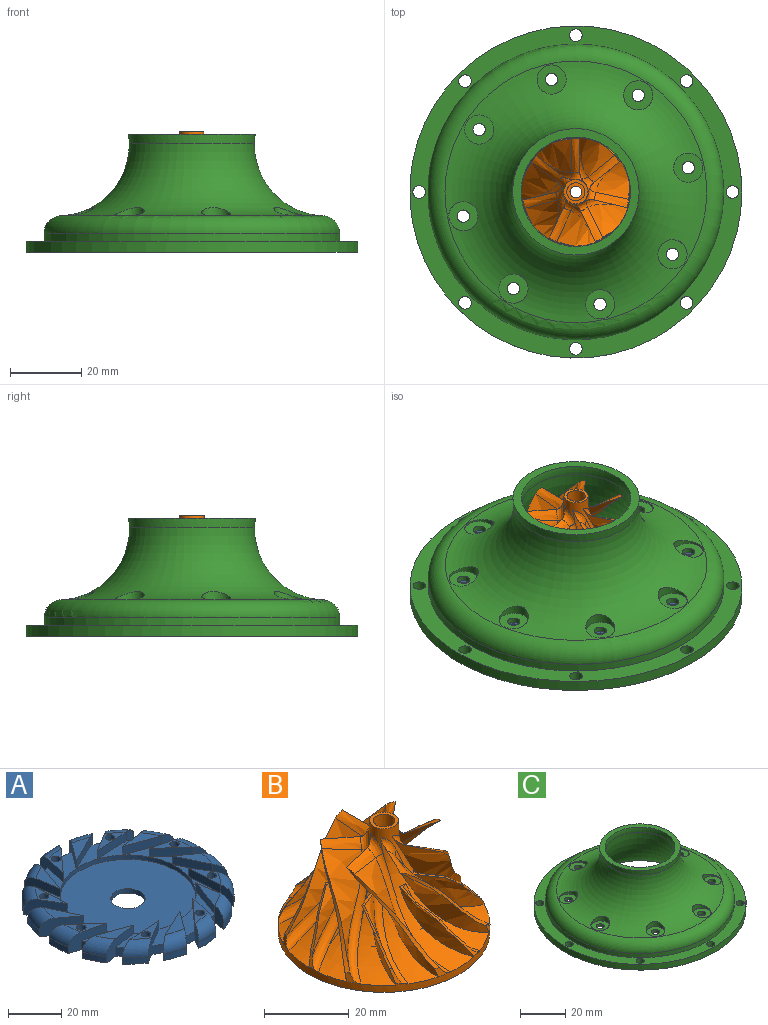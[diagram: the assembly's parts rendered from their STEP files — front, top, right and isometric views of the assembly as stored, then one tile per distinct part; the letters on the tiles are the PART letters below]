
ASSEMBLY  parts=3 mates=1
PART A: 140 faces, bbox 81x81x7.9 mm
  f0: plane 80x80mm, normal (0,0,-1), area 4366.8mm2, adj f1,f2,f3,f4,f5,f6,f7,f8
  f1: cylinder r=35mm len=4.02mm, axis (0,0,1), area 21.5mm2, adj f0,f17,f64,f85
  f2: cylinder r=35mm len=5.08mm, axis (0,0,1), area 21.5mm2, adj f0,f19,f62,f84
  f3: cylinder r=35mm len=5.37mm, axis (0,0,1), area 21.5mm2, adj f0,f20,f60,f99
  f4: cylinder r=35mm len=4.85mm, axis (0,0,1), area 21.5mm2, adj f0,f21,f58,f98
  f5: cylinder r=35mm len=4.02mm, axis (0,0,1), area 21.5mm2, adj f0,f22,f56,f97
  f6: cylinder r=35mm len=5.08mm, axis (0,0,1), area 21.5mm2, adj f0,f23,f54,f96
  f7: cylinder r=35mm len=5.37mm, axis (0,0,1), area 21.5mm2, adj f0,f24,f52,f95
  f8: cylinder r=35mm len=4.85mm, axis (0,0,1), area 21.5mm2, adj f0,f25,f50,f94
  f9: cylinder r=35mm len=4.02mm, axis (0,0,1), area 21.5mm2, adj f0,f26,f48,f93
  f10: cylinder r=35mm len=5.08mm, axis (0,0,1), area 21.5mm2, adj f0,f27,f46,f92
  f11: cylinder r=35mm len=5.37mm, axis (0,0,1), area 21.5mm2, adj f0,f28,f44,f91
  f12: cylinder r=35mm len=4.85mm, axis (0,0,1), area 21.5mm2, adj f0,f29,f42,f90
  f13: cylinder r=35mm len=4.02mm, axis (0,0,1), area 21.5mm2, adj f0,f30,f40,f89
  f14: cylinder r=35mm len=5.08mm, axis (0,0,1), area 21.5mm2, adj f0,f31,f38,f88
  f15: cylinder r=35mm len=5.37mm, axis (0,0,1), area 21.5mm2, adj f0,f32,f36,f87
  f16: cylinder r=35mm len=4.85mm, axis (0,0,1), area 21.5mm2, adj f0,f18,f66,f86
  f17: plane 19.86x5.71mm, normal (0,0,1), area 65.9mm2, adj f1,f35,f64,f67
  f18: plane 19.57x8.16mm, normal (0,0,1), area 65.9mm2, adj f16,f35,f37,f66
  f19: plane 17.11x10.57mm, normal (0,0,1), area 65.9mm2, adj f2,f35,f62,f65
  f20: plane 16.31x12.08mm, normal (0,0,1), area 65.9mm2, adj f3,f35,f60,f63
  f21: plane 19.57x8.16mm, normal (0,0,1), area 65.9mm2, adj f4,f35,f58,f61
  f22: plane 19.86x5.71mm, normal (0,0,1), area 65.9mm2, adj f5,f35,f56,f59
  f23: plane 17.11x10.57mm, normal (0,0,1), area 65.9mm2, adj f6,f35,f54,f57
  f24: plane 16.31x12.08mm, normal (0,0,1), area 65.9mm2, adj f7,f35,f52,f55
  f25: plane 19.57x8.16mm, normal (0,0,1), area 65.9mm2, adj f8,f35,f50,f53
  f26: plane 19.86x5.71mm, normal (0,0,1), area 65.9mm2, adj f9,f35,f48,f51
  f27: plane 17.11x10.57mm, normal (0,0,1), area 65.9mm2, adj f10,f35,f46,f49
  f28: plane 16.31x12.08mm, normal (0,0,1), area 65.9mm2, adj f11,f35,f44,f47
  f29: plane 19.57x8.16mm, normal (0,0,1), area 65.9mm2, adj f12,f35,f42,f45
  f30: plane 19.86x5.71mm, normal (0,0,1), area 65.9mm2, adj f13,f35,f40,f43
  f31: plane 17.11x10.57mm, normal (0,0,1), area 65.9mm2, adj f14,f35,f38,f41
  f32: plane 16.31x12.08mm, normal (0,0,1), area 65.9mm2, adj f15,f35,f36,f39
  f33: plane 51.42x51.42mm, normal (0,0,1), area 1943.8mm2, adj f34,f35
  f34: cylinder r=6.5mm len=13mm, axis (0,0,1), area 81.7mm2, adj f0,f33
  f35: cylinder r=25.71mm len=51.42mm, axis (0,0,-1), area 323.1mm2, adj f17,f18,f19,f20,f21,f22,f23,f24
  f36: plane 13.56x9.97mm, normal (-0.59,-0.81,0), area 82.1mm2, adj f0,f15,f32,f37,f68,f109,f127
  f37: plane 14.73x6.97mm, normal (0.9,0.43,0), area 63.5mm2, adj f18,f36,f86,f109
  f38: plane 16.35x7.9mm, normal (-0.24,-0.97,0), area 82.1mm2, adj f0,f14,f31,f39,f69,f117,f126
  f39: plane 12.07x10.94mm, normal (0.67,0.74,0), area 63.5mm2, adj f32,f38,f87,f117
  f40: plane 16.64x7.9mm, normal (0.15,-0.99,0), area 82.1mm2, adj f0,f13,f30,f41,f70,f110,f125
  f41: plane 15.34x5.49mm, normal (0.34,0.94,0), area 63.5mm2, adj f31,f40,f88,f110
  f42: plane 14.4x8.72mm, normal (0.52,-0.86,0), area 82.1mm2, adj f0,f12,f29,f43,f71,f118,f124
  f43: plane 16.27x3.9mm, normal (-0.05,1,0), area 63.5mm2, adj f30,f42,f89,f118
  f44: plane 13.56x9.97mm, normal (0.81,-0.59,0), area 82.1mm2, adj f0,f11,f28,f45,f72,f111,f139
  f45: plane 14.73x6.97mm, normal (-0.43,0.9,0), area 63.5mm2, adj f29,f44,f90,f111
  f46: plane 16.35x7.9mm, normal (0.97,-0.24,0), area 82.1mm2, adj f0,f10,f27,f47,f73,f119,f138
  f47: plane 12.07x10.94mm, normal (-0.74,0.67,0), area 63.5mm2, adj f28,f46,f91,f119
  f48: plane 16.64x7.9mm, normal (0.99,0.15,0), area 82.1mm2, adj f0,f9,f26,f49,f74,f112,f137
  f49: plane 15.34x5.49mm, normal (-0.94,0.34,0), area 63.5mm2, adj f27,f48,f92,f112
  f50: plane 14.4x8.72mm, normal (0.86,0.52,0), area 82.1mm2, adj f0,f8,f25,f51,f75,f120,f136
  f51: plane 16.27x3.9mm, normal (-1,-0.05,0), area 63.5mm2, adj f26,f50,f93,f120
  f52: plane 13.56x9.97mm, normal (0.59,0.81,0), area 82.1mm2, adj f0,f7,f24,f53,f76,f113,f135
  f53: plane 14.73x6.97mm, normal (-0.9,-0.43,0), area 63.5mm2, adj f25,f52,f94,f113
  f54: plane 16.35x7.9mm, normal (0.24,0.97,0), area 82.1mm2, adj f0,f6,f23,f55,f77,f121,f134
  f55: plane 12.07x10.94mm, normal (-0.67,-0.74,0), area 63.5mm2, adj f24,f54,f95,f121
  f56: plane 16.64x7.9mm, normal (-0.15,0.99,0), area 82.1mm2, adj f0,f5,f22,f57,f78,f114,f133
  f57: plane 15.34x5.49mm, normal (-0.34,-0.94,0), area 63.5mm2, adj f23,f56,f96,f114
  f58: plane 14.4x8.72mm, normal (-0.52,0.86,0), area 82.1mm2, adj f0,f4,f21,f59,f79,f122,f132
  f59: plane 16.27x3.9mm, normal (0.05,-1,0), area 63.5mm2, adj f22,f58,f97,f122
  f60: plane 13.56x9.97mm, normal (-0.81,0.59,0), area 82.1mm2, adj f0,f3,f20,f61,f80,f115,f131
  f61: plane 14.73x6.97mm, normal (0.43,-0.9,0), area 63.5mm2, adj f21,f60,f98,f115
  f62: plane 16.35x7.9mm, normal (-0.97,0.24,0), area 82.1mm2, adj f0,f2,f19,f63,f81,f123,f130
  f63: plane 12.07x10.94mm, normal (0.74,-0.67,0), area 63.5mm2, adj f20,f62,f99,f123
  f64: plane 16.64x7.9mm, normal (-0.99,-0.15,0), area 82.1mm2, adj f0,f1,f17,f65,f82,f108,f129
  f65: plane 15.34x5.49mm, normal (0.94,-0.34,0), area 63.5mm2, adj f19,f64,f84,f108
  f66: plane 14.4x8.72mm, normal (-0.86,-0.52,0), area 82.1mm2, adj f0,f16,f18,f67,f83,f116,f128
  f67: plane 16.27x3.9mm, normal (1,0.05,0), area 63.5mm2, adj f17,f66,f85,f116
  f68: cylinder r=40mm len=9.3mm, axis (0,0,-1), area 28.5mm2, adj f0,f36,f86,f127
  f69: cylinder r=40mm len=9.79mm, axis (0,0,-1), area 28.5mm2, adj f0,f38,f87,f126
  f70: cylinder r=40mm len=8.79mm, axis (0,0,-1), area 28.5mm2, adj f0,f40,f88,f125
  f71: cylinder r=40mm len=7.4mm, axis (0,0,-1), area 28.5mm2, adj f0,f42,f89,f124
  f72: cylinder r=40mm len=9.3mm, axis (0,0,-1), area 28.5mm2, adj f0,f44,f90,f139
  f73: cylinder r=40mm len=9.79mm, axis (0,0,-1), area 28.5mm2, adj f0,f46,f91,f138
  f74: cylinder r=40mm len=8.79mm, axis (0,0,-1), area 28.5mm2, adj f0,f48,f92,f137
  f75: cylinder r=40mm len=7.4mm, axis (0,0,-1), area 28.5mm2, adj f0,f50,f93,f136
  f76: cylinder r=40mm len=9.3mm, axis (0,0,-1), area 28.5mm2, adj f0,f52,f94,f135
  f77: cylinder r=40mm len=9.79mm, axis (0,0,-1), area 28.5mm2, adj f0,f54,f95,f134
  f78: cylinder r=40mm len=8.79mm, axis (0,0,-1), area 28.5mm2, adj f0,f56,f96,f133
  f79: cylinder r=40mm len=7.4mm, axis (0,0,-1), area 28.5mm2, adj f0,f58,f97,f132
  f80: cylinder r=40mm len=9.3mm, axis (0,0,-1), area 28.5mm2, adj f0,f60,f98,f131
  f81: cylinder r=40mm len=9.79mm, axis (0,0,-1), area 28.5mm2, adj f0,f62,f99,f130
  f82: cylinder r=40mm len=8.79mm, axis (0,0,-1), area 28.5mm2, adj f0,f64,f84,f129
  f83: cylinder r=40mm len=7.4mm, axis (0,0,-1), area 28.5mm2, adj f0,f66,f85,f128
  f84: plane 7.9x5.67mm, normal (0.99,-0.13,0), area 39.1mm2, adj f0,f2,f65,f82,f129
  f85: plane 7.9x5.53mm, normal (0.97,0.26,0), area 39.1mm2, adj f0,f1,f67,f83,f128
  f86: plane 7.9x4.54mm, normal (0.79,0.61,0), area 39.1mm2, adj f0,f16,f37,f68,f127
  f87: plane 7.9x4.95mm, normal (0.5,0.87,0), area 39.1mm2, adj f0,f15,f39,f69,f126
  f88: plane 7.9x5.67mm, normal (0.13,0.99,0), area 39.1mm2, adj f0,f14,f41,f70,f125
  f89: plane 7.9x5.53mm, normal (-0.26,0.97,0), area 39.1mm2, adj f0,f13,f43,f71,f124
  f90: plane 7.9x4.54mm, normal (-0.61,0.79,0), area 39.1mm2, adj f0,f12,f45,f72,f139
  f91: plane 7.9x4.95mm, normal (-0.87,0.5,0), area 39.1mm2, adj f0,f11,f47,f73,f138
  f92: plane 7.9x5.67mm, normal (-0.99,0.13,0), area 39.1mm2, adj f0,f10,f49,f74,f137
  f93: plane 7.9x5.53mm, normal (-0.97,-0.26,0), area 39.1mm2, adj f0,f9,f51,f75,f136
  f94: plane 7.9x4.54mm, normal (-0.79,-0.61,0), area 39.1mm2, adj f0,f8,f53,f76,f135
  f95: plane 7.9x4.95mm, normal (-0.5,-0.87,0), area 39.1mm2, adj f0,f7,f55,f77,f134
  f96: plane 7.9x5.67mm, normal (-0.13,-0.99,0), area 39.1mm2, adj f0,f6,f57,f78,f133
  f97: plane 7.9x5.53mm, normal (0.26,-0.97,0), area 39.1mm2, adj f0,f5,f59,f79,f132
  f98: plane 7.9x4.54mm, normal (0.61,-0.79,0), area 39.1mm2, adj f0,f4,f61,f80,f131
  f99: plane 7.9x4.95mm, normal (0.87,-0.5,0), area 39.1mm2, adj f0,f3,f63,f81,f130
  f100: cylinder r=1.75mm len=7.9mm, axis (0,0,1), area 86.9mm2, adj f0,f116
  f101: cylinder r=1.75mm len=7.9mm, axis (0,0,1), area 86.9mm2, adj f0,f123
  f102: cylinder r=1.75mm len=7.9mm, axis (0,0,1), area 86.9mm2, adj f0,f122
  f103: cylinder r=1.75mm len=7.9mm, axis (0,0,1), area 86.9mm2, adj f0,f121
  f104: cylinder r=1.75mm len=7.9mm, axis (0,0,1), area 86.9mm2, adj f0,f120
  f105: cylinder r=1.75mm len=7.9mm, axis (0,0,1), area 86.9mm2, adj f0,f119
  f106: cylinder r=1.75mm len=7.9mm, axis (0,0,1), area 86.9mm2, adj f0,f118
  f107: cylinder r=1.75mm len=7.9mm, axis (0,0,1), area 86.9mm2, adj f0,f117
  f108: plane 15.34x7.18mm, normal (0,0,1), area 44.9mm2, adj f64,f65,f129
  f109: plane 14.73x9.06mm, normal (0,0,1), area 44.9mm2, adj f36,f37,f127
  f110: plane 15.34x7.18mm, normal (0,0,1), area 44.9mm2, adj f40,f41,f125
  f111: plane 14.73x9.06mm, normal (0,0,1), area 44.9mm2, adj f44,f45,f139
  f112: plane 15.34x7.18mm, normal (0,0,1), area 44.9mm2, adj f48,f49,f137
  f113: plane 14.73x9.06mm, normal (0,0,1), area 44.9mm2, adj f52,f53,f135
  f114: plane 15.34x7.18mm, normal (0,0,1), area 44.9mm2, adj f56,f57,f133
  f115: plane 14.73x9.06mm, normal (0,0,1), area 44.9mm2, adj f60,f61,f131
  f116: plane 16.27x5.82mm, normal (0,0,1), area 35.3mm2, adj f66,f67,f100,f128
  f117: plane 12.07x10.94mm, normal (0,0,1), area 35.3mm2, adj f38,f39,f107,f126
  f118: plane 16.27x5.82mm, normal (0,0,1), area 35.3mm2, adj f42,f43,f106,f124
  f119: plane 12.07x10.94mm, normal (0,0,1), area 35.3mm2, adj f46,f47,f105,f138
  f120: plane 16.27x5.82mm, normal (0,0,1), area 35.3mm2, adj f50,f51,f104,f136
  f121: plane 12.07x10.94mm, normal (0,0,1), area 35.3mm2, adj f54,f55,f103,f134
  f122: plane 16.27x5.82mm, normal (0,0,1), area 35.3mm2, adj f58,f59,f102,f132
  f123: plane 12.07x10.94mm, normal (0,0,1), area 35.3mm2, adj f62,f63,f101,f130
  f124: torus R=35mm, axis (0,0,1), area 73.1mm2, adj f42,f71,f89,f118
  f125: torus R=35mm, axis (0,0,1), area 73.1mm2, adj f40,f70,f88,f110
  f126: torus R=35mm, axis (0,0,1), area 73.1mm2, adj f38,f69,f87,f117
  f127: torus R=35mm, axis (0,0,1), area 73.1mm2, adj f36,f68,f86,f109
  f128: torus R=35mm, axis (0,0,1), area 73.1mm2, adj f66,f83,f85,f116
  f129: torus R=35mm, axis (0,0,1), area 73.1mm2, adj f64,f82,f84,f108
  f130: torus R=35mm, axis (0,0,1), area 73.1mm2, adj f62,f81,f99,f123
  f131: torus R=35mm, axis (0,0,1), area 73.1mm2, adj f60,f80,f98,f115
  f132: torus R=35mm, axis (0,0,1), area 73.1mm2, adj f58,f79,f97,f122
  f133: torus R=35mm, axis (0,0,1), area 73.1mm2, adj f56,f78,f96,f114
  f134: torus R=35mm, axis (0,0,1), area 73.1mm2, adj f54,f77,f95,f121
  f135: torus R=35mm, axis (0,0,1), area 73.1mm2, adj f52,f76,f94,f113
  f136: torus R=35mm, axis (0,0,1), area 73.1mm2, adj f50,f75,f93,f120
  f137: torus R=35mm, axis (0,0,1), area 73.1mm2, adj f48,f74,f92,f112
  f138: torus R=35mm, axis (0,0,1), area 73.1mm2, adj f46,f73,f91,f119
  f139: torus R=35mm, axis (0,0,1), area 73.1mm2, adj f44,f72,f90,f111
PART B: 110 faces, bbox 96.8x96.8x57.1 mm
  f0: bspline ~8.36x7mm, area 3.9mm2, adj f7,f20,f39,f50,f76
  f1: bspline ~8.36x7.68mm, area 3.9mm2, adj f8,f19,f39,f53,f75
  f2: bspline ~3.52x3.19mm, area 3.9mm2, adj f9,f18,f39,f56,f74
  f3: bspline ~8.36x6.86mm, area 3.9mm2, adj f10,f17,f39,f59,f73
  f4: bspline ~8.36x8.15mm, area 3.9mm2, adj f11,f16,f39,f62,f72
  f5: bspline ~8.36x5.88mm, area 3.5mm2, adj f12,f15,f39,f40,f65,f71
  f6: bspline ~3.37x3.19mm, area 3.9mm2, adj f13,f14,f39,f68,f70
  f7: bspline ~20.21x15mm, area 105.9mm2, adj f0,f39,f43,f49,f51,f76
  f8: bspline ~20.21x15mm, area 105.9mm2, adj f1,f39,f43,f52,f54,f75
  f9: bspline ~18.13x15mm, area 105.9mm2, adj f2,f39,f43,f55,f57,f74
  f10: bspline ~19.19x15mm, area 105.9mm2, adj f3,f39,f43,f58,f60,f73
  f11: bspline ~15x14.27mm, area 105.9mm2, adj f4,f39,f43,f61,f63,f72
  f12: bspline ~18.97x15mm, area 105.9mm2, adj f5,f40,f43,f64,f66,f71
  f13: bspline ~18.13x15mm, area 105.9mm2, adj f6,f39,f42,f67,f69,f70
  f14: bspline ~18.5x17.17mm, area 69.7mm2, adj f6,f39,f42,f67,f68
  f15: bspline ~20.78x17.17mm, area 69.7mm2, adj f5,f39,f43,f44,f64,f65
  f16: bspline ~17.35x16.96mm, area 69.7mm2, adj f4,f39,f43,f61,f62
  f17: bspline ~21.06x17.17mm, area 69.7mm2, adj f3,f39,f43,f58,f59
  f18: bspline ~17.85x17.35mm, area 69.7mm2, adj f2,f39,f43,f55,f56
  f19: bspline ~20.29x17.17mm, area 69.7mm2, adj f1,f39,f43,f52,f53
  f20: bspline ~19.5x17.17mm, area 69.7mm2, adj f0,f39,f43,f49,f50
  f21: bspline ~27.7x27.53mm, area 243.9mm2, adj f22,f43,f83,f84,f92
  f22: bspline ~2.79x2.23mm, area 4.5mm2, adj f21,f39,f83,f91
  f23: bspline ~26.51x25mm, area 111.4mm2, adj f83,f84,f91
  f24: bspline ~27.83x27.7mm, area 243.9mm2, adj f25,f43,f82,f85,f94
  f25: bspline ~11.94x7.96mm, area 4.5mm2, adj f24,f39,f82,f93
  f26: bspline ~25.5x25mm, area 111.4mm2, adj f82,f85,f93
  f27: bspline ~28.67x27.7mm, area 243.9mm2, adj f28,f43,f81,f86,f96
  f28: bspline ~2.5x2.29mm, area 4.5mm2, adj f27,f39,f81,f95
  f29: bspline ~25.46x25.31mm, area 111.4mm2, adj f81,f86,f95
  f30: bspline ~27.7x27.14mm, area 243.9mm2, adj f31,f43,f80,f87,f98
  f31: bspline ~3.35x2.23mm, area 4.5mm2, adj f30,f39,f80,f97
  f32: bspline ~25x24.99mm, area 111.4mm2, adj f80,f87,f97
  f33: bspline ~29.69x27.48mm, area 243.9mm2, adj f34,f43,f79,f88,f100
  f34: bspline ~11.94x8.06mm, area 4.5mm2, adj f33,f39,f79,f99
  f35: bspline ~26.82x25mm, area 111.4mm2, adj f79,f88,f99
  f36: bspline ~27.48x26.83mm, area 244mm2, adj f37,f42,f43,f78,f89,f102
  f37: bspline ~11.94x6.3mm, area 4.5mm2, adj f36,f39,f78,f101
  f38: bspline ~26.38x25mm, area 111.4mm2, adj f78,f89,f101
  f39: cylinder r=25mm len=50mm, axis (0,0,-1), area 321.7mm2, adj f0,f1,f2,f3,f4,f5,f6,f7
  f40: cylinder r=25mm len=0.35mm, axis (0,0,-1), area 0mm2, adj f5,f12,f39
  f41: plane 50x50mm, normal (0,0,-1), area 1868.2mm2, adj f39,f109
  f42: torus R=34.04mm, axis (0,0,-1), area 222.6mm2, adj f13,f14,f36,f39,f43,f67,f103
  f43: torus R=34.04mm, axis (0,0,-1), area 1298.9mm2, adj f7,f8,f9,f10,f11,f12,f15,f16
  f44: torus R=34.04mm, axis (0,0,-1), area 73.9mm2, adj f15,f39,f43,f48
  f45: plane 6.82x6.82mm, normal (0,0,1), area 15.8mm2, adj f43,f105
  f46: bspline ~26.83x25mm, area 111.4mm2, adj f77,f90,f103
  f47: bspline ~3.25x2.23mm, area 4.5mm2, adj f39,f48,f77,f103
  f48: bspline ~29.6x27.7mm, area 246.6mm2, adj f43,f44,f47,f77,f90,f104
  f49: plane 7.64x4.37mm, normal (0,0,1), area 5.2mm2, adj f7,f20,f43,f50,f51
  f50: bspline ~14.71x12.78mm, area 63.2mm2, adj f0,f20,f49,f51,f76
  f51: bspline ~4.9x4.51mm, area 3.9mm2, adj f7,f49,f50,f76
  f52: plane 7.84x5.09mm, normal (0,0,1), area 5.2mm2, adj f8,f19,f43,f53,f54
  f53: bspline ~15.5x12.78mm, area 63.2mm2, adj f1,f19,f52,f54,f75
  f54: bspline ~6.13x4.9mm, area 3.9mm2, adj f8,f52,f53,f75
  f55: plane 8.06x2.72mm, normal (0,0,1), area 5.2mm2, adj f9,f18,f43,f56,f57
  f56: bspline ~12.92x12.78mm, area 63.2mm2, adj f2,f18,f55,f57,f74
  f57: bspline ~5.08x4.9mm, area 3.9mm2, adj f9,f55,f56,f74
  f58: plane 7x6.26mm, normal (0,0,1), area 5.2mm2, adj f10,f17,f43,f59,f60
  f59: bspline ~16.03x12.78mm, area 63.2mm2, adj f3,f17,f58,f60,f73
  f60: bspline ~5.88x4.9mm, area 3.9mm2, adj f10,f58,f59,f73
  f61: plane 8.36x2.12mm, normal (0,0,1), area 5.2mm2, adj f11,f16,f43,f62,f63
  f62: bspline ~12.78x12.16mm, area 63.2mm2, adj f4,f16,f61,f63,f72
  f63: bspline ~5.72x4.9mm, area 3.9mm2, adj f11,f61,f62,f72
  f64: plane 7.12x5.82mm, normal (0,0,1), area 5.2mm2, adj f12,f15,f43,f65,f66
  f65: bspline ~15.77x12.78mm, area 63.2mm2, adj f5,f15,f64,f66,f71
  f66: bspline ~5.33x4.9mm, area 3.9mm2, adj f12,f64,f65,f71
  f67: plane 8.3x3.69mm, normal (0,0,1), area 5.2mm2, adj f13,f14,f42,f68,f69
  f68: bspline ~14.18x12.78mm, area 63.2mm2, adj f6,f14,f67,f69,f70
  f69: bspline ~6.08x4.9mm, area 3.9mm2, adj f13,f67,f68,f70
  f70: torus R=44.59mm, axis (0,0,1), area 5.5mm2, adj f6,f13,f68,f69
  f71: torus R=44.59mm, axis (0,0,1), area 5.5mm2, adj f5,f12,f65,f66
  f72: torus R=44.59mm, axis (0,0,1), area 5.5mm2, adj f4,f11,f62,f63
  f73: torus R=44.59mm, axis (0,0,1), area 5.5mm2, adj f3,f10,f59,f60
  f74: torus R=44.59mm, axis (0,0,1), area 5.5mm2, adj f2,f9,f56,f57
  f75: torus R=44.59mm, axis (0,0,1), area 5.5mm2, adj f1,f8,f53,f54
  f76: torus R=44.59mm, axis (0,0,1), area 5.5mm2, adj f0,f7,f50,f51
  f77: torus R=44.59mm, axis (0,0,1), area 26.1mm2, adj f46,f47,f48,f90,f103
  f78: torus R=44.59mm, axis (0,0,1), area 26.1mm2, adj f36,f37,f38,f89,f101
  f79: torus R=44.59mm, axis (0,0,1), area 26.1mm2, adj f33,f34,f35,f88,f99
  f80: torus R=44.59mm, axis (0,0,1), area 26.1mm2, adj f30,f31,f32,f87,f97
  f81: torus R=44.59mm, axis (0,0,1), area 26.1mm2, adj f27,f28,f29,f86,f95
  f82: torus R=44.59mm, axis (0,0,1), area 26.1mm2, adj f24,f25,f26,f85,f93
  f83: torus R=44.59mm, axis (0,0,1), area 26.1mm2, adj f21,f22,f23,f84,f91
  f84: bspline ~10.21x2.41mm, area 28mm2, adj f21,f23,f83,f92
  f85: bspline ~12.02x9.85mm, area 28mm2, adj f24,f26,f82,f94
  f86: bspline ~12.06x4.89mm, area 28mm2, adj f27,f29,f81,f96
  f87: bspline ~12.27x7.26mm, area 28mm2, adj f30,f32,f80,f98
  f88: bspline ~11.68x7.39mm, area 28mm2, adj f33,f35,f79,f100
  f89: bspline ~10.45x4.42mm, area 28mm2, adj f36,f38,f78,f102
  f90: bspline ~11.54x10.2mm, area 28mm2, adj f46,f48,f77,f104
  f91: bspline ~25.41x25.03mm, area 85.4mm2, adj f22,f23,f39,f43,f83,f92
  f92: bspline ~5.89x5.71mm, area 12mm2, adj f21,f43,f84,f91
  f93: bspline ~25.41x23.42mm, area 85.4mm2, adj f25,f26,f39,f43,f82,f94
  f94: bspline ~5.71x4.82mm, area 12mm2, adj f24,f43,f85,f93
  f95: bspline ~25.41x23.28mm, area 85.4mm2, adj f28,f29,f39,f43,f81,f96
  f96: bspline ~5.84x5.71mm, area 12mm2, adj f27,f43,f86,f95
  f97: bspline ~25.41x25.23mm, area 85.4mm2, adj f31,f32,f39,f43,f80,f98
  f98: bspline ~5.71x5.15mm, area 12mm2, adj f30,f43,f87,f97
  f99: bspline ~25.41x20.74mm, area 85.4mm2, adj f34,f35,f39,f43,f79,f100
  f100: bspline ~5.71x5.49mm, area 12mm2, adj f33,f43,f88,f99
  f101: bspline ~25.78x25.41mm, area 85.4mm2, adj f37,f38,f39,f43,f78,f102
  f102: bspline ~5.71x5.65mm, area 12mm2, adj f36,f43,f89,f101
  f103: bspline ~25.41x20.44mm, area 85.4mm2, adj f39,f42,f43,f46,f47,f77,f104
  f104: bspline ~5.71x4.87mm, area 12mm2, adj f43,f48,f90,f103
  f105: cylinder r=2.56mm len=15mm, axis (0,0,1), area 241.6mm2, adj f45,f106
  f106: plane 5.13x5.13mm, normal (0,0,1), area 12.1mm2, adj f105,f107
  f107: cylinder r=1.65mm len=17.5mm, axis (0,0,-1), area 181.4mm2, adj f106,f108
  f108: plane 6.66x6.66mm, normal (0,0,-1), area 26.2mm2, adj f107,f109
  f109: torus R=5.51mm, axis (0,0,1), area 62.3mm2, adj f41,f108
PART C: 51 faces, bbox 93.5x93.5x52.3 mm
  f0: cylinder r=1.75mm len=3.5mm, axis (0,0,-1), area 16.5mm2, adj f11,f50
  f1: cylinder r=1.75mm len=3.5mm, axis (0,0,-1), area 16.5mm2, adj f11,f48
  f2: cylinder r=1.75mm len=3.5mm, axis (0,0,-1), area 16.5mm2, adj f11,f46
  f3: cylinder r=1.75mm len=3.5mm, axis (0,0,-1), area 16.5mm2, adj f11,f44
  f4: cylinder r=1.75mm len=3.5mm, axis (0,0,-1), area 16.5mm2, adj f11,f42
  f5: cylinder r=1.75mm len=3.5mm, axis (0,0,-1), area 16.5mm2, adj f11,f40
  f6: cylinder r=1.75mm len=3.5mm, axis (0,0,-1), area 16.5mm2, adj f11,f38
  f7: cylinder r=1.75mm len=3.5mm, axis (0,0,-1), area 16.5mm2, adj f11,f36
  f8: cylinder r=46.75mm len=93.5mm, axis (0,0,1), area 905.4mm2, adj f9,f17,f29,f30,f31,f32
  f9: plane 93.5x93.5mm, normal (0,0,-1), area 1683mm2, adj f8,f10,f20,f21,f22,f23,f24,f25
  f10: cylinder r=40.3mm len=80.61mm, axis (0,0,1), area 861.1mm2, adj f9,f28
  f11: plane 70.61x70.61mm, normal (0,0,-1), area 1891.3mm2, adj f0,f1,f2,f3,f4,f5,f6,f7
  f12: torus R=29.4mm, axis (0,0,1), area 257.5mm2, adj f11,f13
  f13: torus R=46.17mm, axis (0,0,1), area 2641.8mm2, adj f12,f14
  f14: torus R=27.44mm, axis (0,0,1), area 263.4mm2, adj f13,f34
  f15: torus R=45.29mm, axis (0,0,1), area 288.2mm2, adj f19,f34
  f16: cylinder r=41.65mm len=83.3mm, axis (0,0,1), area 584.1mm2, adj f17,f18
  f17: plane 93.5x93.5mm, normal (0,0,1), area 1337.1mm2, adj f8,f16,f20,f21,f22,f23,f24,f25
  f18: torus R=36.65mm, axis (0,0,1), area 1920.6mm2, adj f16,f19
  f19: torus R=37.62mm, axis (0,0,1), area 4332.9mm2, adj f15,f18,f35,f37,f39,f41,f43,f45
  f20: cylinder r=1.78mm len=3.56mm, axis (0,0,1), area 34.5mm2, adj f9,f17
  f21: cylinder r=1.78mm len=3.56mm, axis (0,0,1), area 34.5mm2, adj f9,f17
  f22: cylinder r=1.78mm len=3.56mm, axis (0,0,1), area 34.5mm2, adj f9,f17
  f23: cylinder r=1.78mm len=3.56mm, axis (0,0,1), area 34.5mm2, adj f9,f17
  f24: cylinder r=1.78mm len=3.56mm, axis (0,0,1), area 34.5mm2, adj f9,f17
  f25: cylinder r=1.78mm len=3.56mm, axis (0,0,1), area 34.5mm2, adj f9,f17
  f26: cylinder r=1.78mm len=3.56mm, axis (0,0,1), area 34.5mm2, adj f9,f17
  f27: cylinder r=1.78mm len=3.56mm, axis (0,0,1), area 34.5mm2, adj f9,f17
  f28: torus R=35.3mm, axis (0,0,1), area 1899.3mm2, adj f10,f11
  f29: plane 1.21x0.25mm, normal (0,0,-1), area 0.3mm2, adj f8,f30,f32,f33
  f30: plane 0.82x0.25mm, normal (0,1,0), area 0.2mm2, adj f8,f29,f31,f33
  f31: plane 1.21x0.25mm, normal (0,0,1), area 0.3mm2, adj f8,f30,f32,f33
  f32: plane 0.82x0.23mm, normal (0,-1,0), area 0.2mm2, adj f8,f29,f31,f33
  f33: plane 1.21x0.82mm, normal (1,0,0), area 1mm2, adj f29,f30,f31,f32
  f34: plane 35.6x35.6mm, normal (0,0,1), area 248.5mm2, adj f14,f15
  f35: cylinder r=4.11mm len=8.23mm, axis (0,0,1), area 33.6mm2, adj f19,f36
  f36: plane 8.23x8.23mm, normal (0,0,1), area 43.5mm2, adj f7,f35
  f37: cylinder r=4.11mm len=8.23mm, axis (0,0,1), area 33.6mm2, adj f19,f38
  f38: plane 8.23x8.23mm, normal (0,0,1), area 43.5mm2, adj f6,f37
  f39: cylinder r=4.11mm len=8.23mm, axis (0,0,1), area 33.6mm2, adj f19,f40
  f40: plane 8.23x8.23mm, normal (0,0,1), area 43.5mm2, adj f5,f39
  f41: cylinder r=4.11mm len=8.23mm, axis (0,0,1), area 33.6mm2, adj f19,f42
  f42: plane 8.23x8.23mm, normal (0,0,1), area 43.5mm2, adj f4,f41
  f43: cylinder r=4.11mm len=8.23mm, axis (0,0,1), area 33.6mm2, adj f19,f44
  f44: plane 8.23x8.23mm, normal (0,0,1), area 43.5mm2, adj f3,f43
  f45: cylinder r=4.11mm len=8.23mm, axis (0,0,1), area 33.6mm2, adj f19,f46
  f46: plane 8.23x8.23mm, normal (0,0,1), area 43.5mm2, adj f2,f45
  f47: cylinder r=4.11mm len=8.23mm, axis (0,0,1), area 33.6mm2, adj f19,f48
  f48: plane 8.23x8.23mm, normal (0,0,1), area 43.5mm2, adj f1,f47
  f49: cylinder r=4.11mm len=8.23mm, axis (0,0,1), area 33.6mm2, adj f19,f50
  f50: plane 8.23x8.23mm, normal (0,0,1), area 43.5mm2, adj f0,f49
PLACE A t=(-9.06,-9.68,-7.82)mm
PLACE B t=(-9.06,-9.68,-8.82)mm
PLACE C t=(-9.06,-9.68,-7.42)mm
MATE fastened C.f8 <-> A.f81  axis (0,0,-1) through (-9.06,-9.68,-10.82)mm
